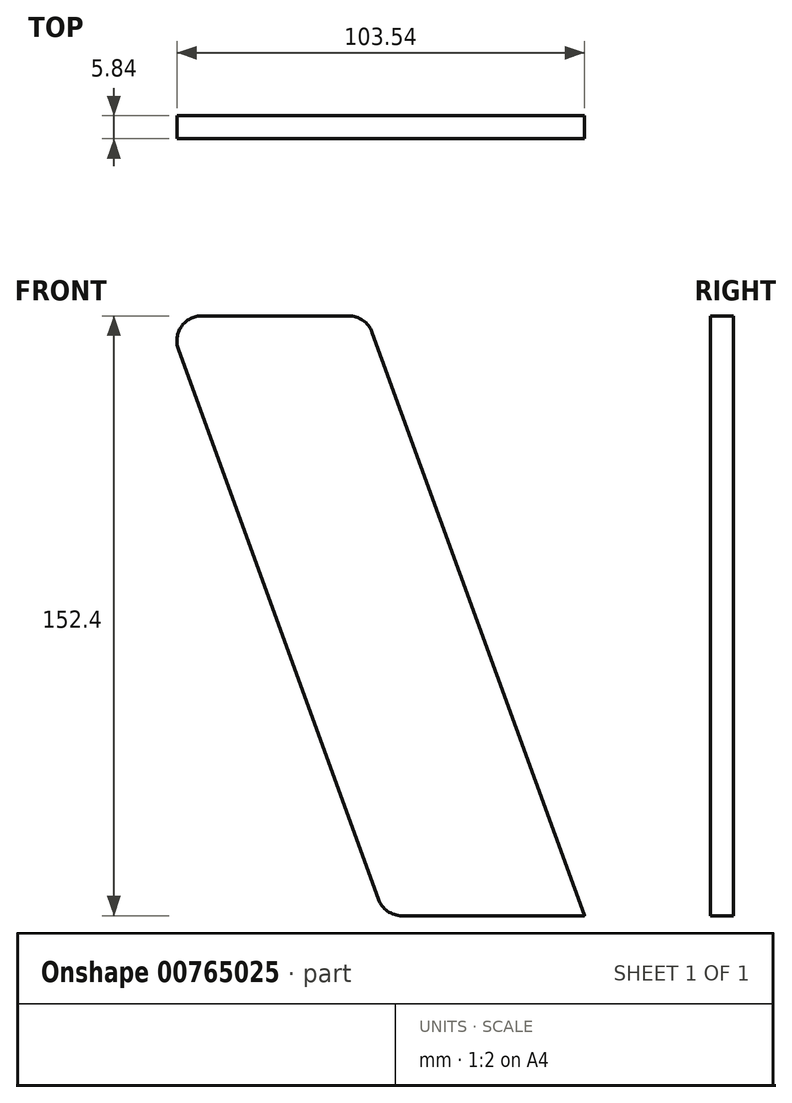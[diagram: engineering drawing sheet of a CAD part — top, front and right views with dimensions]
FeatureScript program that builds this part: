
annotation { "Feature Type Name" : "Feature", "Feature Type Description" : "" }
export const myFeature = defineFeature(function(context is Context, id is Id, definition is map)
    precondition{}
    {
        {
            var Q0;
            Q0=qCreatedBy(makeId("Front.planeOp"),FACE);
            var sketch = newSketch(context, id + "F0", { "sketchPlane" : qUnion([Q0])});
            skLineSegment(sketch, "E0", {"start": v(0, 0) * mm, "end": v(50.8, 0) * mm});
            skLineSegment(sketch, "E1", {"start": v(50.8, 0) * mm, "end": v(106.27, -152.4) * mm});
            skLineSegment(sketch, "E2", {"start": v(106.27, -152.4) * mm, "end": v(55.47, -152.4) * mm});
            skLineSegment(sketch, "E3", {"start": v(55.47, -152.4) * mm, "end": v(0, 0) * mm});
            skSolve(sketch);
        }
        {
            var Q0;
            Q0 = qSketchRegion(id + "F0", true);
            extrude(context, id + "F1", {"entities" : qUnion([Q0]), "depth" : 5.84 * mm, "offsetDistance" : 25.4 * mm});
        }
        {
            var Q0;
            Q0=makeQuery(id+"F1.opExtrude","SWEPT_EDGE",EDGE,{"disambiguationData":[OSD([sQuery(id+"F0.wireOp",EDGE,"E2"),sQuery(id+"F0.wireOp",EDGE,"E3")])]});
            var Q1;
            Q1=makeQuery(id+"F1.opExtrude","SWEPT_EDGE",EDGE,{"disambiguationData":[OSD([sQuery(id+"F0.wireOp",EDGE,"E0"),sQuery(id+"F0.wireOp",EDGE,"E1")])]});
            var Q2;
            Q2=makeQuery(id+"F1.opExtrude","SWEPT_EDGE",EDGE,{"disambiguationData":[OSD([sQuery(id+"F0.wireOp",EDGE,"E0"),sQuery(id+"F0.wireOp",EDGE,"E3")])]});
            fillet(context, id + "F2", {"entities" : qUnion([Q0, Q1, Q2]), "radius" : 6.35 * mm, "tangentPropagation" : true, "allowEdgeOverflow" : false});
        }
        {
            var Q0;
            Q0=makeQuery(id+"F1.opExtrude","SWEPT_EDGE",EDGE,{"disambiguationData":[OSD([sQuery(id+"F0.wireOp",EDGE,"E1"),sQuery(id+"F0.wireOp",EDGE,"E2")])]});
            fillet(context, id + "F3", {"entities" : qUnion([Q0]), "radius" : 1 / 50.8 * mm, "tangentPropagation" : true, "allowEdgeOverflow" : false});
        }
    });
